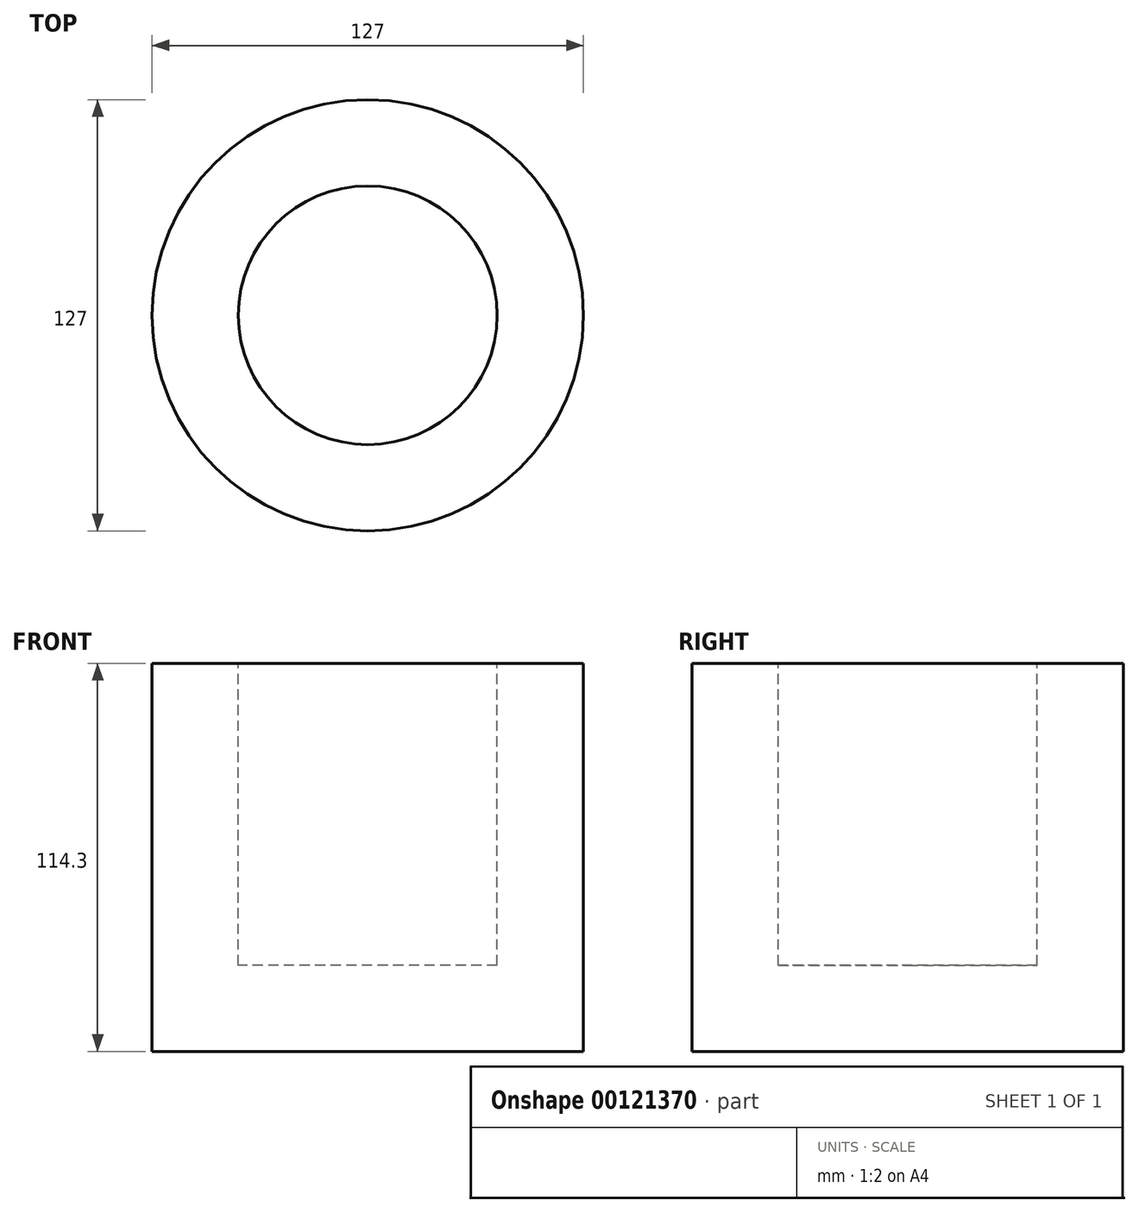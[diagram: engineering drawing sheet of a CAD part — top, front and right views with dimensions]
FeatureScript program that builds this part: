
annotation { "Feature Type Name" : "Feature", "Feature Type Description" : "" }
export const myFeature = defineFeature(function(context is Context, id is Id, definition is map)
    precondition{}
    {
        {
            var Q0;
            Q0=qCreatedBy(makeId("Front.planeOp"),FACE);
            var sketch = newSketch(context, id + "F0", { "sketchPlane" : qUnion([Q0])});
            skLineSegment(sketch, "E0", {"start": v(0, 0) * mm, "end": v(0, 114.3) * mm});
            skLineSegment(sketch, "E1", {"start": v(0, 114.3) * mm, "end": v(25.4, 114.3) * mm});
            skLineSegment(sketch, "E2", {"start": v(25.4, 114.3) * mm, "end": v(25.4, 25.4) * mm});
            skLineSegment(sketch, "E3", {"start": v(25.4, 25.4) * mm, "end": v(63.5, 25.4) * mm});
            skLineSegment(sketch, "E4", {"start": v(63.5, 25.4) * mm, "end": v(63.5, 0) * mm});
            skLineSegment(sketch, "E5", {"start": v(63.5, 0) * mm, "end": v(0, 0) * mm});
            skSolve(sketch);
        }
        {
            var Q0;
            Q0=makeQuery(id+"F0.imprint","IMPRINT",FACE,{"disambiguationData":[TD([[makeQuery(id+"F0.imprint","IMPRINT",EDGE,{"derivedFrom":sQuery(id+"F0.wireOp",EDGE,"E0")}),-1.0]])]});
            var Q1;
            Q1=sQuery(id+"F0.wireOp",EDGE,"E4");
            revolve(context, id + "F1", {"entities" : qUnion([Q0]), "axis" : qUnion([Q1]), "revolveType" : RevolveType.FULL});
        }
    });
